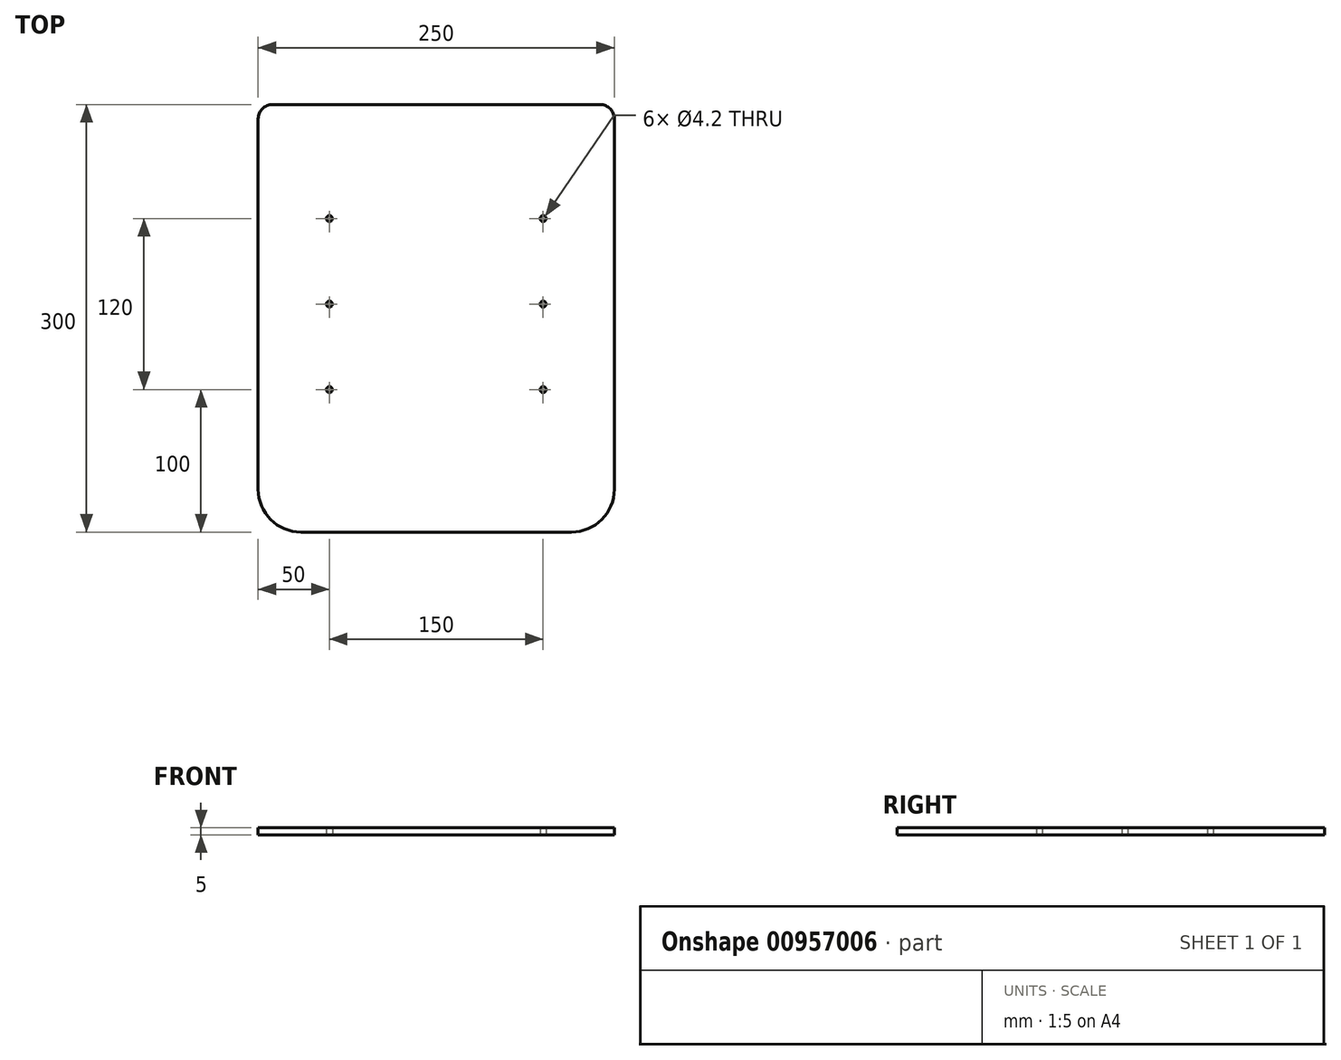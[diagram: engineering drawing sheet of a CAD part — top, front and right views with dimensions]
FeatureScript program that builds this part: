
annotation { "Feature Type Name" : "Feature", "Feature Type Description" : "" }
export const myFeature = defineFeature(function(context is Context, id is Id, definition is map)
    precondition{}
    {
        {
            var Q0;
            Q0=qCreatedBy(makeId("Top.planeOp"),FACE);
            var sketch = newSketch(context, id + "F0", { "sketchPlane" : qUnion([Q0])});
            skLineSegment(sketch, "E0.bottom", {"start": v(0, 0) * mm, "end": v(250, 0) * mm});
            skLineSegment(sketch, "E0.top", {"start": v(0, 300) * mm, "end": v(250, 300) * mm});
            skLineSegment(sketch, "E0.left", {"start": v(0, 0) * mm, "end": v(0, 300) * mm});
            skLineSegment(sketch, "E0.right", {"start": v(250, 0) * mm, "end": v(250, 300) * mm});
            skSolve(sketch);
        }
        {
            var Q0;
            Q0 = qSketchRegion(id + "F0", true);
            extrude(context, id + "F1", {"entities" : qUnion([Q0]), "depth" : 5 * mm, "offsetDistance" : 25 * mm});
        }
        {
            var Q0;
            Q0=qCreatedBy(makeId("Top.planeOp"),FACE);
            var sketch = newSketch(context, id + "F2", { "sketchPlane" : qUnion([Q0])});
            skPoint(sketch, "E1", {"position": v(50, 100) * mm});
            skPoint(sketch, "E2", {"position": v(50, 160) * mm});
            skPoint(sketch, "E3", {"position": v(50, 220) * mm});
            skLineSegment(sketch, "E4", {"start": v(125, 300) * mm, "end": v(125, 0) * mm});
            skPoint(sketch, "E5.MirrorP", {"position": v(200, 220) * mm});
            skPoint(sketch, "E6.MirrorP", {"position": v(200, 160) * mm});
            skPoint(sketch, "E7.MirrorP", {"position": v(200, 100) * mm});
            skSolve(sketch);
        }
        {
            var Q0;
            Q0=sQuery(id+"F2.wireOp",VERTEX,"E3");
            var Q1;
            Q1=sQuery(id+"F2.wireOp",VERTEX,"E2");
            var Q2;
            Q2=sQuery(id+"F2.wireOp",VERTEX,"E5.MirrorP");
            var Q3;
            Q3=sQuery(id+"F2.wireOp",VERTEX,"E6.MirrorP");
            var Q4;
            Q4=sQuery(id+"F2.wireOp",VERTEX,"E7.MirrorP");
            var Q5;
            Q5=sQuery(id+"F2.wireOp",VERTEX,"E1");
            var Q6;
            Q6=makeQuery(id+"F1.opExtrude","SWEPT_BODY",BODY,{"disambiguationData":[OSD([sQuery(id+"F0.wireOp",EDGE,"E0.bottom"),sQuery(id+"F0.wireOp",EDGE,"E0.top"),sQuery(id+"F0.wireOp",EDGE,"E0.left"),sQuery(id+"F0.wireOp",EDGE,"E0.right")])]});
            hole(context, id + "F3", {"style" : HoleStyle.SIMPLE, "endStyle" : HoleEndStyle.THROUGH, "oppositeDirection" : true, "standardTappedOrClearance" : lookupTablePath({ "standard" : "ISO", "engagement" : "75%", "pitch" : "0.8 mm", "size" : "M5", "type" : "Tapped" }), "standardBlindInLast" : lookupTablePath({ "standard" : "ISO", "fit" : "Normal", "engagement" : "75%", "pitch" : "0.8 mm", "size" : "M5", "type" : "Clearance & tapped" }), "holeDiameter" : 4.2 * mm, "majorDiameter" : 5 * mm, "showTappedDepth" : true, "isTappedThrough" : true, "tappedDepth" : 12 * mm, "tapClearance" : 3, "locations" : qUnion([Q0, Q1, Q2, Q3, Q4, Q5]), "scope" : qUnion([Q6])});
        }
        {
            var Q0;
            Q0=makeQuery(id+"F1.opExtrude","SWEPT_EDGE",EDGE,{"disambiguationData":[OSD([sQuery(id+"F0.wireOp",EDGE,"E0.top"),sQuery(id+"F0.wireOp",EDGE,"E0.left")])]});
            var Q1;
            Q1=makeQuery(id+"F1.opExtrude","SWEPT_EDGE",EDGE,{"disambiguationData":[OSD([sQuery(id+"F0.wireOp",EDGE,"E0.top"),sQuery(id+"F0.wireOp",EDGE,"E0.right")])]});
            fillet(context, id + "F4", {"entities" : qUnion([Q0, Q1]), "radius" : 10 * mm, "tangentPropagation" : true, "allowEdgeOverflow" : false});
        }
        {
            var Q0;
            Q0=makeQuery(id+"F1.opExtrude","SWEPT_EDGE",EDGE,{"disambiguationData":[OSD([sQuery(id+"F0.wireOp",EDGE,"E0.bottom"),sQuery(id+"F0.wireOp",EDGE,"E0.left")])]});
            var Q1;
            Q1=makeQuery(id+"F1.opExtrude","SWEPT_EDGE",EDGE,{"disambiguationData":[OSD([sQuery(id+"F0.wireOp",EDGE,"E0.bottom"),sQuery(id+"F0.wireOp",EDGE,"E0.right")])]});
            fillet(context, id + "F5", {"entities" : qUnion([Q0, Q1]), "radius" : 30 * mm, "tangentPropagation" : true, "allowEdgeOverflow" : false});
        }
    });
